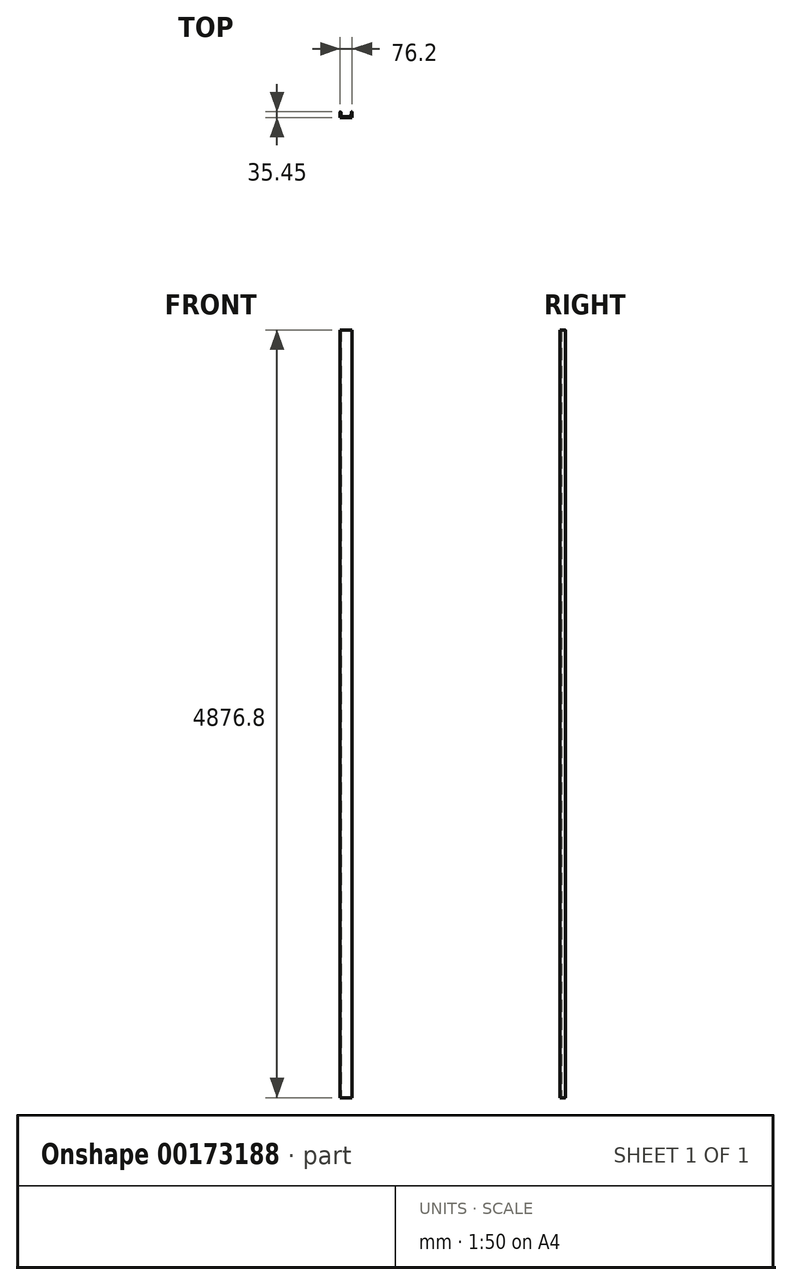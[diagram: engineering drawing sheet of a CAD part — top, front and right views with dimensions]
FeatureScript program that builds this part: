
annotation { "Feature Type Name" : "Feature", "Feature Type Description" : "" }
export const myFeature = defineFeature(function(context is Context, id is Id, definition is map)
    precondition{}
    {
        {
            var Q0;
            Q0=qCreatedBy(makeId("Top.planeOp"),FACE);
            var sketch = newSketch(context, id + "F0", { "sketchPlane" : qUnion([Q0])});
            skLineSegment(sketch, "E0", {"start": v(-33.57, 0) * mm, "end": v(42.63, 0) * mm});
            skLineSegment(sketch, "E1", {"start": v(42.63, 0) * mm, "end": v(42.63, 32.96) * mm});
            skLineSegment(sketch, "E2", {"start": v(-33.57, 0) * mm, "end": v(-33.57, 32.96) * mm});
            skLineSegment(sketch, "E3.0", {"start": v(-19.53, 4.34) * mm, "end": v(28.58, 4.34) * mm});
            skArc(sketch, "E4.filletArc", {"start": v(-26.64, 11.46) * mm, "mid": v(-24.56, 6.43) * mm, "end": v(-19.53, 4.34) * mm});
            skArc(sketch, "E5.filletArc", {"start": v(28.58, 4.34) * mm, "mid": v(33.6, 6.43) * mm, "end": v(35.7, 11.46) * mm});
            skLineSegment(sketch, "E6", {"start": v(-28.59, 33.18) * mm, "end": v(-26.64, 11.46) * mm});
            skLineSegment(sketch, "E7", {"start": v(35.7, 11.46) * mm, "end": v(37.64, 33.18) * mm});
            skArc(sketch, "E8.filletArc", {"start": v(-28.59, 33.18) * mm, "mid": v(-31.19, 35.45) * mm, "end": v(-33.57, 32.96) * mm});
            skArc(sketch, "E9.filletArc", {"start": v(42.63, 32.96) * mm, "mid": v(40.24, 35.45) * mm, "end": v(37.64, 33.18) * mm});
            skSolve(sketch);
        }
        {
            var Q0;
            Q0=makeQuery(id+"F0.imprint","IMPRINT",FACE,{"disambiguationData":[TD([[makeQuery(id+"F0.imprint","IMPRINT",EDGE,{"derivedFrom":sQuery(id+"F0.wireOp",EDGE,"E0")}),1.0]])]});
            extrude(context, id + "F1", {"entities" : qUnion([Q0]), "depth" : 4876.8 * mm});
        }
    });
